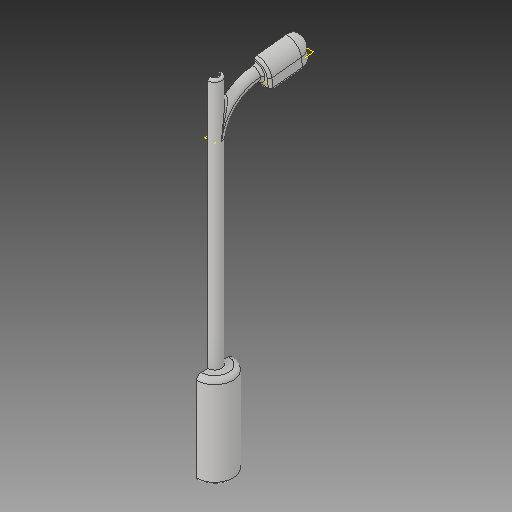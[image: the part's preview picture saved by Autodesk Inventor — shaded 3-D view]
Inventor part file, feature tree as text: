
AUTODESK INVENTOR PART (.ipt)
format: ipt  version: 2018 (Build 220112000, 112)  size: 292,352 bytes
history: native  units: in
note: dims shown in document units (in); Inventor stores cm internally (conversion verified against a paired STEP export)
features: sketch x10, other x3, plane x1
ambient origin geometry x8: Origin, YZ Plane, XZ Plane, XY Plane, X Axis, Y Axis, Z Axis, Center Point
bodies: Solid1 (feature_tree)
feature tree (14):
  other  "lampa.ipt"
  other  "Solid1::lampa.ipt"
  other  "TaggingFeature1"
  sketch  "Sketch1"  dims[d0=0.3937in]
  sketch  "Sketch6"
  sketch  "Sketch8"
  sketch  "Sketch9"
  sketch  "Sketch10"
  sketch  "Sketch11"
  sketch  "Sketch12"
  sketch  "Sketch13"
  sketch  "Sketch14"
  sketch  "Sketch15"
  plane  "Work Plane1"
